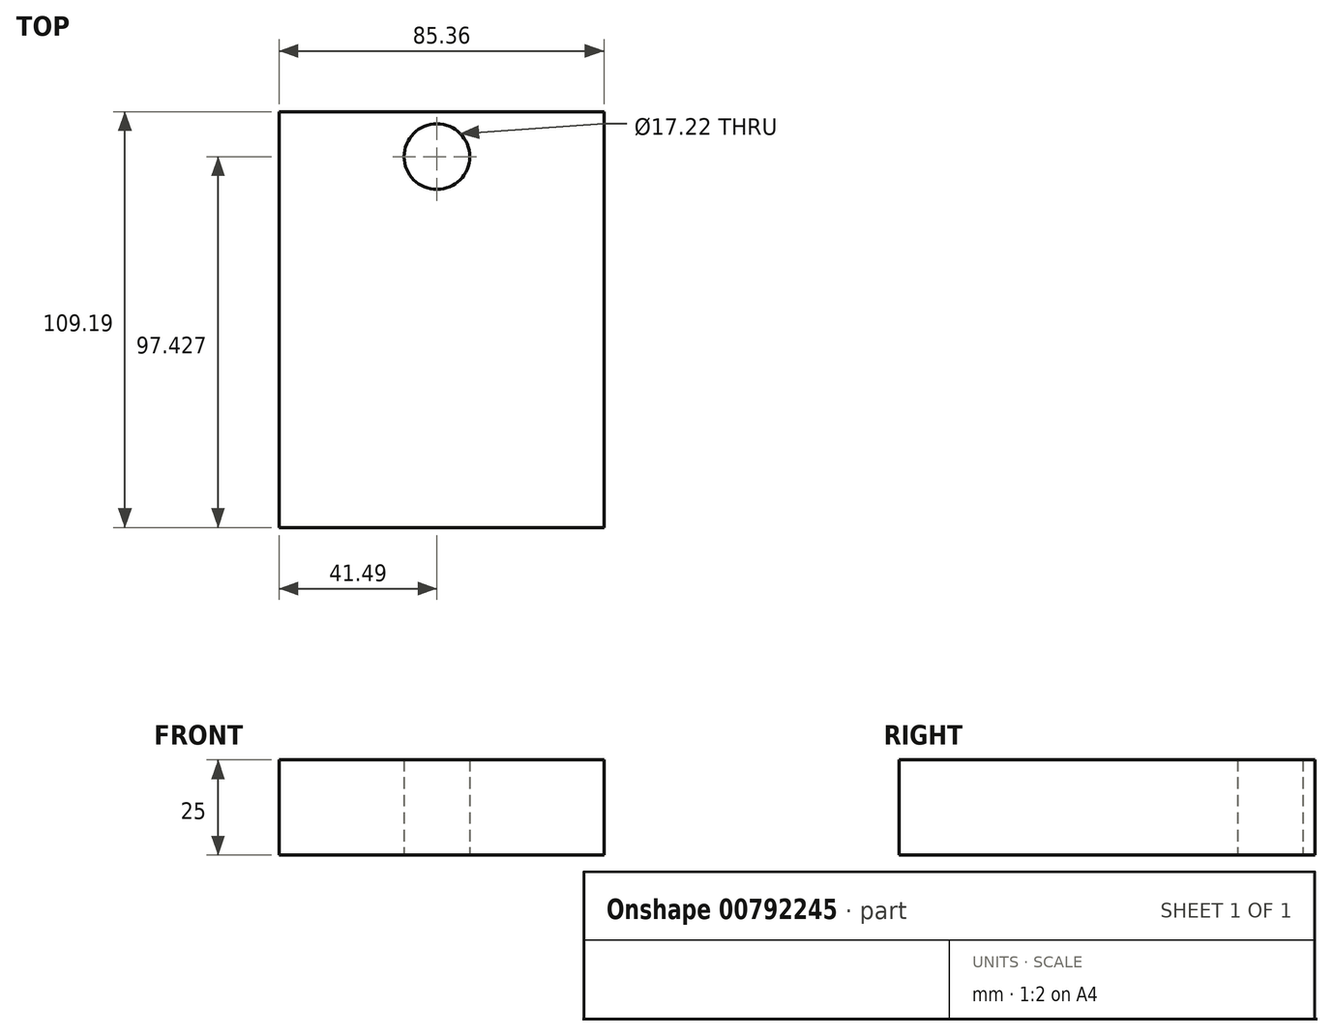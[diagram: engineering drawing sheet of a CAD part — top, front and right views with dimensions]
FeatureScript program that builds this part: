
annotation { "Feature Type Name" : "Feature", "Feature Type Description" : "" }
export const myFeature = defineFeature(function(context is Context, id is Id, definition is map)
    precondition{}
    {
        {
            var Q0;
            Q0=qCreatedBy(makeId("Top.planeOp"),FACE);
            var sketch = newSketch(context, id + "F0", { "sketchPlane" : qUnion([Q0])});
            skLineSegment(sketch, "E0.bottom", {"start": v(-41.49, 56.76) * mm, "end": v(43.87, 56.76) * mm});
            skLineSegment(sketch, "E0.top", {"start": v(-41.49, -52.43) * mm, "end": v(43.87, -52.43) * mm});
            skLineSegment(sketch, "E0.left", {"start": v(-41.49, 56.76) * mm, "end": v(-41.49, -52.43) * mm});
            skLineSegment(sketch, "E0.right", {"start": v(43.87, 56.76) * mm, "end": v(43.87, -52.43) * mm});
            skCircle(sketch, "E1", {"center": v(0, 45) * mm, "radius": 8.6 * mm});
            skCircle(sketch, "E2", {"center": v(0, 45) * mm, "radius": 8 * mm});
            skSolve(sketch);
        }
        {
            var Q0;
            Q0=makeQuery(id+"F0.imprint","IMPRINT",FACE,{"disambiguationData":[TD([[makeQuery(id+"F0.imprint","IMPRINT",EDGE,{"derivedFrom":sQuery(id+"F0.wireOp",EDGE,"E0.bottom")}),-1.0]])]});
            extrude(context, id + "F1", {"entities" : qUnion([Q0]), "depth" : 25 * mm, "offsetDistance" : 25 * mm});
        }
    });
